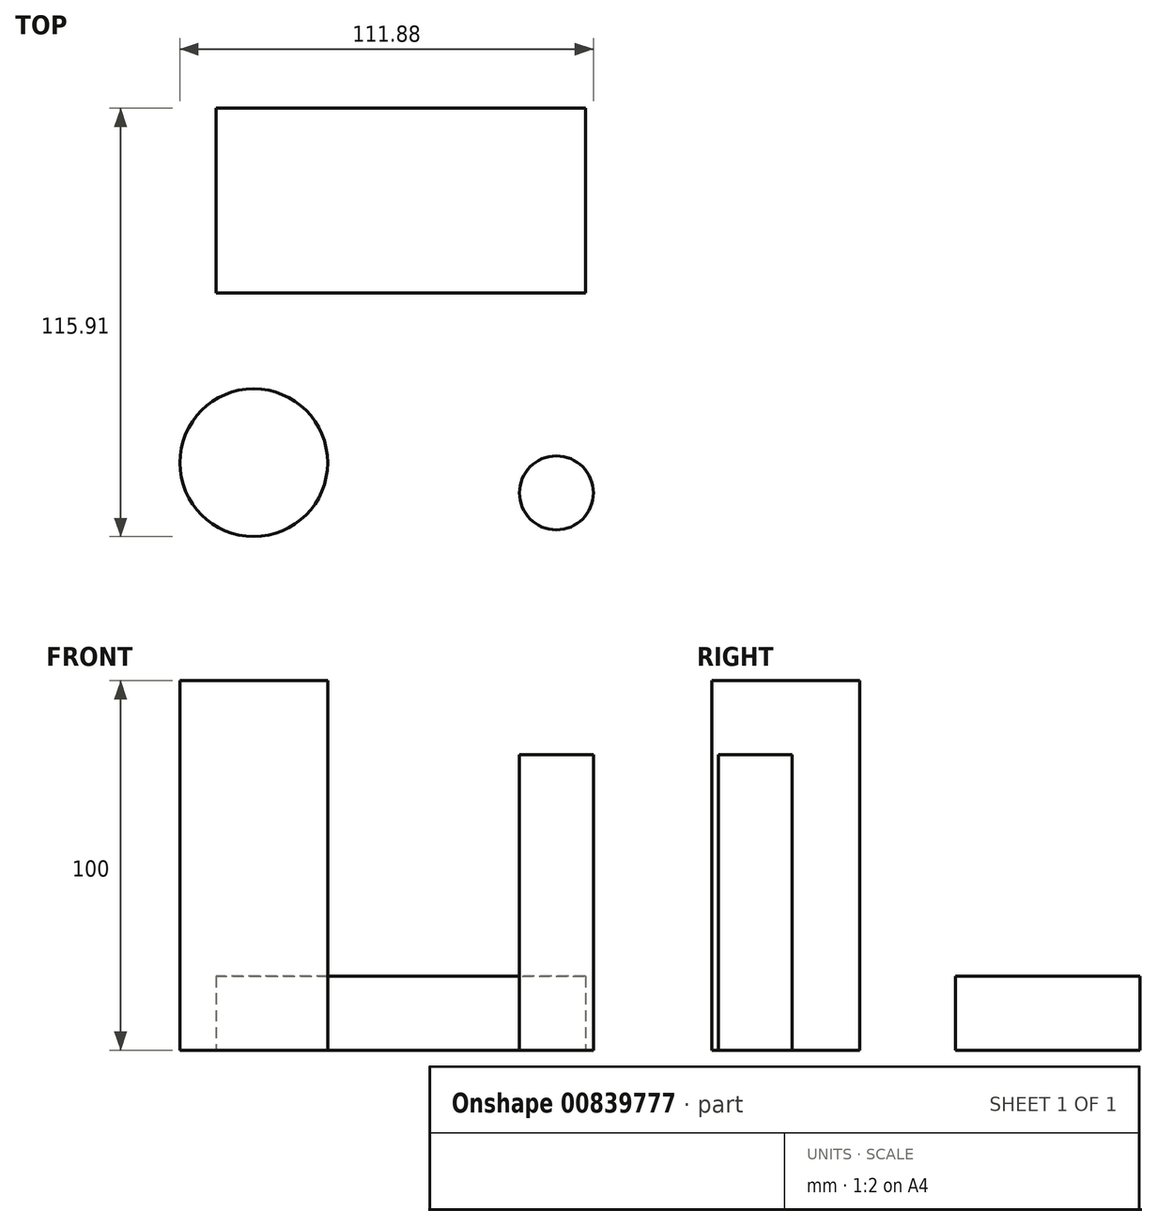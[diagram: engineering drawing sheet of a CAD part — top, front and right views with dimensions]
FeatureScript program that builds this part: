
annotation { "Feature Type Name" : "Feature", "Feature Type Description" : "" }
export const myFeature = defineFeature(function(context is Context, id is Id, definition is map)
    precondition{}
    {
        {
            var Q0;
            Q0=qCreatedBy(makeId("Top.planeOp"),FACE);
            var sketch = newSketch(context, id + "F0", { "sketchPlane" : qUnion([Q0])});
            skLineSegment(sketch, "E0", {"start": v(-43.54, 30.95) * mm, "end": v(-43.54, -19.05) * mm});
            skLineSegment(sketch, "E1", {"start": v(56.46, -19.05) * mm, "end": v(-43.54, -19.05) * mm});
            skLineSegment(sketch, "E2", {"start": v(-43.54, 30.95) * mm, "end": v(56.46, 30.95) * mm});
            skLineSegment(sketch, "E3", {"start": v(56.46, 30.95) * mm, "end": v(56.46, -19.05) * mm});
            skCircle(sketch, "E4", {"center": v(-33.3, -64.96) * mm, "radius": 20 * mm});
            skCircle(sketch, "E5", {"center": v(48.58, -73.13) * mm, "radius": 10 * mm});
            skSolve(sketch);
        }
        {
            var Q0;
            Q0=makeQuery(id+"F0.imprint","IMPRINT",FACE,{"disambiguationData":[TD([[makeQuery(id+"F0.imprint","IMPRINT",EDGE,{"derivedFrom":sQuery(id+"F0.wireOp",EDGE,"E0")}),1.0]])]});
            extrude(context, id + "F1", {"entities" : qUnion([Q0]), "depth" : 20 * mm, "offsetDistance" : 25 * mm});
        }
        {
            var Q0;
            Q0=makeQuery(id+"F0.imprint","IMPRINT",FACE,{"disambiguationData":[TD([[makeQuery(id+"F0.imprint","IMPRINT",EDGE,{"derivedFrom":sQuery(id+"F0.wireOp",EDGE,"E5")}),1.0]])]});
            extrude(context, id + "F2", {"entities" : qUnion([Q0]), "depth" : 80 * mm, "offsetDistance" : 25 * mm});
        }
        {
            var Q0;
            Q0=makeQuery(id+"F0.imprint","IMPRINT",FACE,{"disambiguationData":[TD([[makeQuery(id+"F0.imprint","IMPRINT",EDGE,{"derivedFrom":sQuery(id+"F0.wireOp",EDGE,"E4")}),1.0]])]});
            extrude(context, id + "F3", {"entities" : qUnion([Q0]), "depth" : 100 * mm, "offsetDistance" : 25 * mm});
        }
    });
